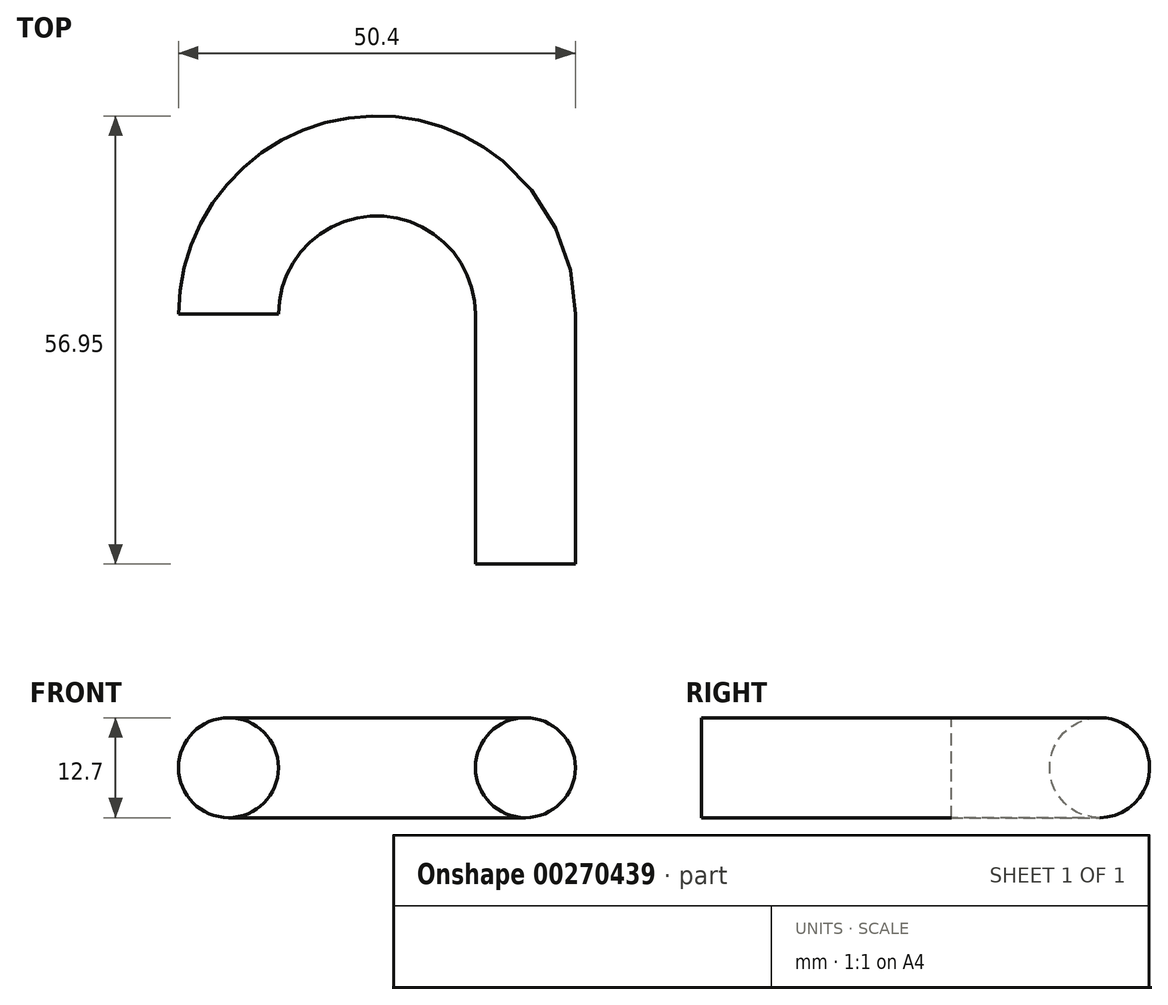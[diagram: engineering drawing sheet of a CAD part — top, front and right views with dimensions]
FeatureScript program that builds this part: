
annotation { "Feature Type Name" : "Feature", "Feature Type Description" : "" }
export const myFeature = defineFeature(function(context is Context, id is Id, definition is map)
    precondition{}
    {
        {
            var Q0;
            Q0=qCreatedBy(makeId("Top.planeOp"),FACE);
            var sketch = newSketch(context, id + "F0", { "sketchPlane" : qUnion([Q0])});
            skLineSegment(sketch, "E0", {"start": v(0, 0) * mm, "end": v(0, 31.75) * mm});
            skArc(sketch, "E1", {"start": v(0, 31.75) * mm, "mid": v(-18.85, 50.6) * mm, "end": v(-37.7, 31.75) * mm});
            skSolve(sketch);
        }
        {
            var Q0;
            Q0=qCreatedBy(makeId("Front.planeOp"),FACE);
            var sketch = newSketch(context, id + "F1", { "sketchPlane" : qUnion([Q0])});
            skCircle(sketch, "E2", {"center": v(0, 0) * mm, "radius": 6.35 * mm});
            skSolve(sketch);
        }
        {
            var Q0;
            Q0=makeQuery(id+"F1.imprint","IMPRINT",FACE,{"disambiguationData":[TD([[makeQuery(id+"F1.imprint","IMPRINT",EDGE,{"derivedFrom":sQuery(id+"F1.wireOp",EDGE,"E2")}),1.0]])]});
            var Q1;
            Q1=sQuery(id+"F0.wireOp",EDGE,"E0");
            var Q2;
            Q2=sQuery(id+"F0.wireOp",EDGE,"E1");
            sweep(context, id + "F2", {"profiles" : qUnion([Q0]), "path" : qUnion([Q1, Q2])});
        }
    });
